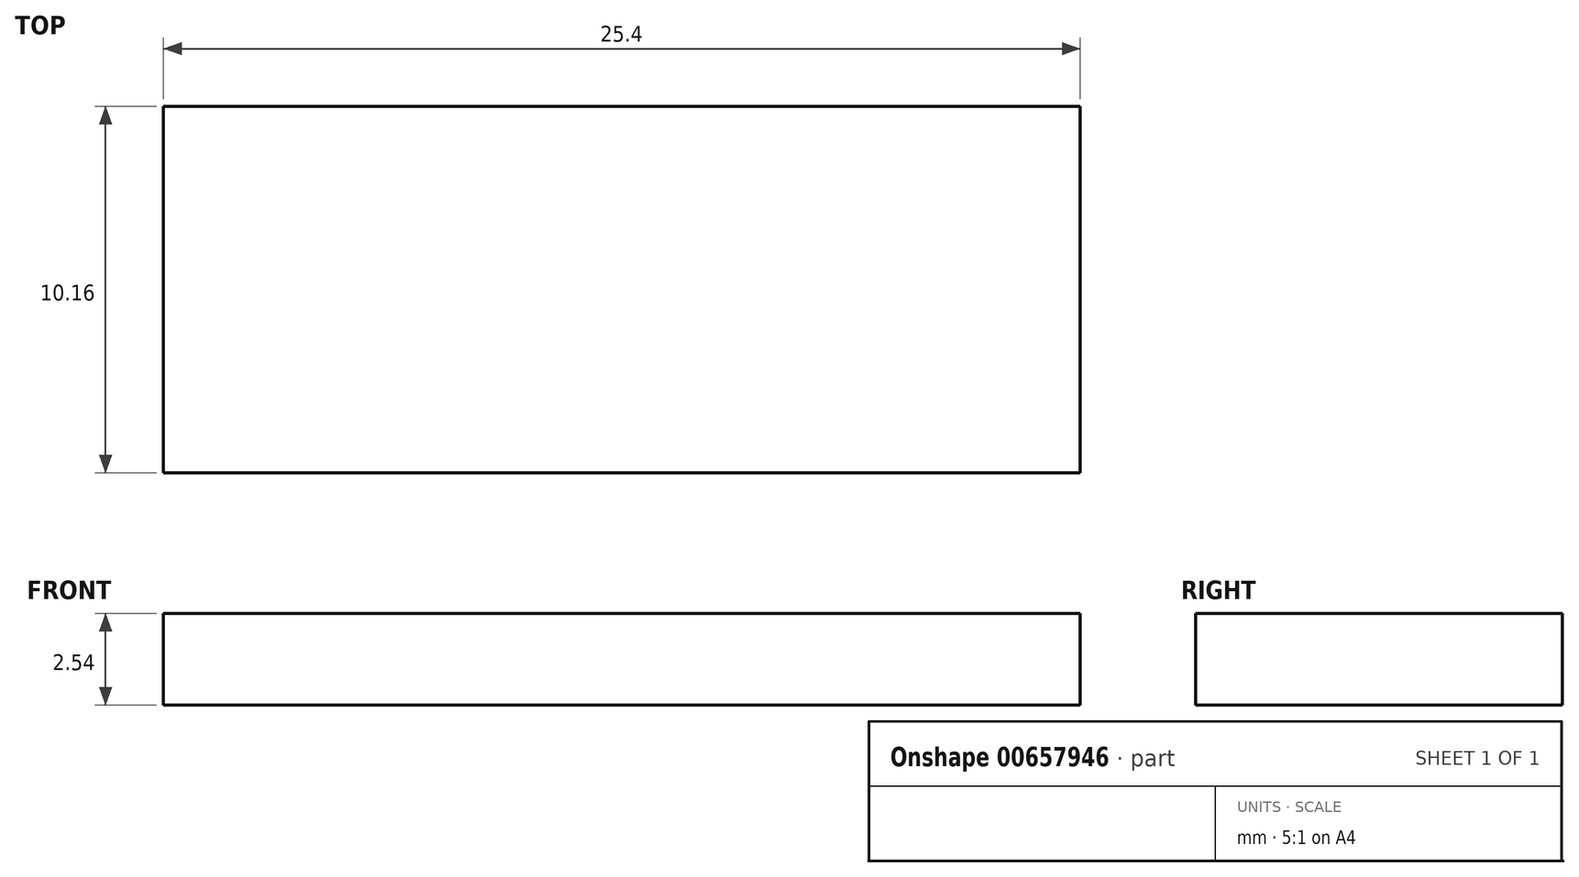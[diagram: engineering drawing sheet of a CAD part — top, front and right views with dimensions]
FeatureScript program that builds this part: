
annotation { "Feature Type Name" : "Feature", "Feature Type Description" : "" }
export const myFeature = defineFeature(function(context is Context, id is Id, definition is map)
    precondition{}
    {
        {
            var Q0;
            Q0=qCreatedBy(makeId("Top.planeOp"),FACE);
            var sketch = newSketch(context, id + "F0", { "sketchPlane" : qUnion([Q0])});
            skLineSegment(sketch, "E0.bottom", {"start": v(-8.24, 7.78) * mm, "end": v(17.16, 7.78) * mm});
            skLineSegment(sketch, "E0.top", {"start": v(-8.24, -2.38) * mm, "end": v(17.16, -2.38) * mm});
            skLineSegment(sketch, "E0.left", {"start": v(-8.24, 7.78) * mm, "end": v(-8.24, -2.38) * mm});
            skLineSegment(sketch, "E0.right", {"start": v(17.16, 7.78) * mm, "end": v(17.16, -2.38) * mm});
            skSolve(sketch);
        }
        {
            var Q0;
            Q0 = qSketchRegion(id + "F0", true);
            extrude(context, id + "F1", {"entities" : qUnion([Q0]), "depth" : 2.54 * mm, "offsetDistance" : 25.4 * mm});
        }
    });
